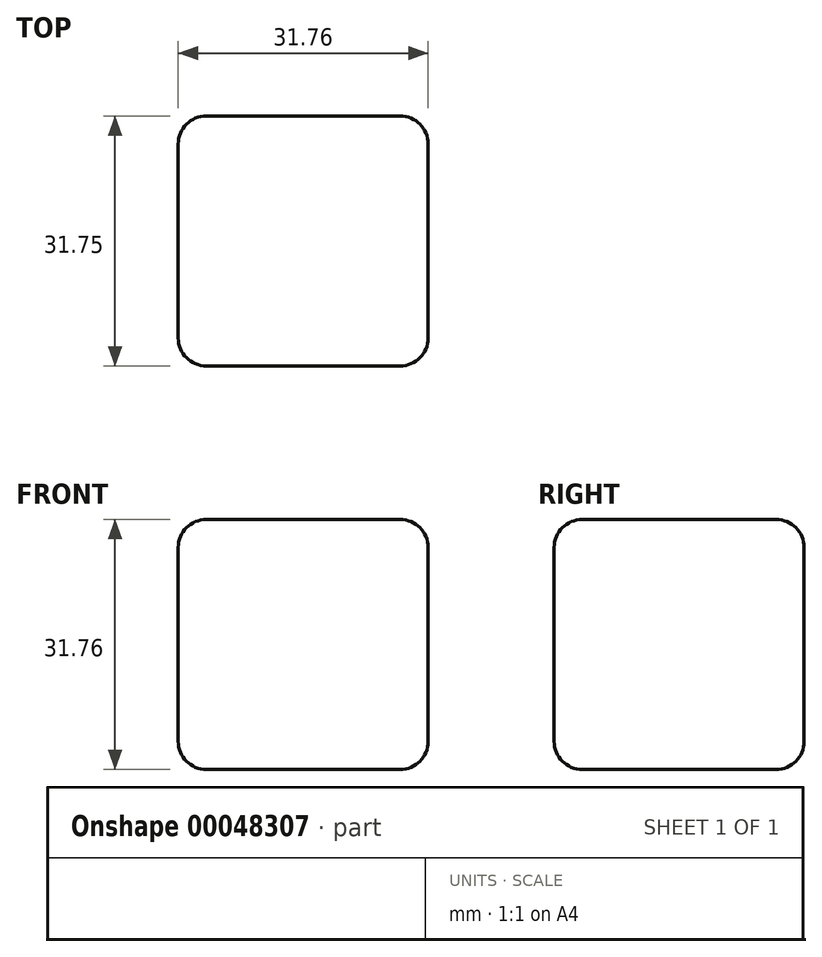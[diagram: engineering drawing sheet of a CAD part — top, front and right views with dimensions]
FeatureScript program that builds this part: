
annotation { "Feature Type Name" : "Feature", "Feature Type Description" : "" }
export const myFeature = defineFeature(function(context is Context, id is Id, definition is map)
    precondition{}
    {
        {
            var Q0;
            Q0=qCreatedBy(makeId("Front.planeOp"),FACE);
            var sketch = newSketch(context, id + "F0", { "sketchPlane" : qUnion([Q0])});
            skLineSegment(sketch, "E0.rect.bottom", {"start": v(15.88, -15.87) * mm, "end": v(-15.88, -15.88) * mm});
            skLineSegment(sketch, "E0.rect.top", {"start": v(15.88, 15.88) * mm, "end": v(-15.88, 15.87) * mm});
            skLineSegment(sketch, "E0.rect.left", {"start": v(15.88, -15.87) * mm, "end": v(15.88, 15.88) * mm});
            skLineSegment(sketch, "E0.rect.right", {"start": v(-15.88, -15.88) * mm, "end": v(-15.88, 15.87) * mm});
            skPoint(sketch, "E0.rect.middle", {"position": v(0, 0) * mm});
            skSolve(sketch);
        }
        {
            var Q0;
            Q0=makeQuery(id+"F0.imprint","IMPRINT",FACE,{"disambiguationData":[TD([[makeQuery(id+"F0.imprint","IMPRINT",EDGE,{"derivedFrom":sQuery(id+"F0.wireOp",EDGE,"E0.rect.bottom")}),-1.0]])]});
            extrude(context, id + "F1", {"entities" : qUnion([Q0]), "depth" : 31.75 * mm});
        }
        {
            var Q0;
            Q0=makeQuery(id+"F1.opExtrude","SWEPT_EDGE",EDGE,{"disambiguationData":[OSD([sQuery(id+"F0.wireOp",EDGE,"E0.rect.bottom"),sQuery(id+"F0.wireOp",EDGE,"E0.rect.left")])]});
            var Q1;
            Q1=makeQuery(id+"F1.opExtrude","CAP_FACE",FACE,{"disambiguationData":[OSD([sQuery(id+"F0.wireOp",EDGE,"E0.rect.bottom"),sQuery(id+"F0.wireOp",EDGE,"E0.rect.top"),sQuery(id+"F0.wireOp",EDGE,"E0.rect.left"),sQuery(id+"F0.wireOp",EDGE,"E0.rect.right")])],"isStart":true});
            var Q2;
            Q2=makeQuery(id+"F1.opExtrude","SWEPT_EDGE",EDGE,{"disambiguationData":[OSD([sQuery(id+"F0.wireOp",EDGE,"E0.rect.bottom"),sQuery(id+"F0.wireOp",EDGE,"E0.rect.right")])]});
            var Q3;
            Q3=makeQuery(id+"F1.opExtrude","CAP_FACE",FACE,{"disambiguationData":[OSD([sQuery(id+"F0.wireOp",EDGE,"E0.rect.bottom"),sQuery(id+"F0.wireOp",EDGE,"E0.rect.top"),sQuery(id+"F0.wireOp",EDGE,"E0.rect.left"),sQuery(id+"F0.wireOp",EDGE,"E0.rect.right")])],"isStart":false});
            var Q4;
            Q4=makeQuery(id+"F1.opExtrude","SWEPT_EDGE",EDGE,{"disambiguationData":[OSD([sQuery(id+"F0.wireOp",EDGE,"E0.rect.top"),sQuery(id+"F0.wireOp",EDGE,"E0.rect.left")])]});
            var Q5;
            Q5=makeQuery(id+"F1.opExtrude","SWEPT_FACE",FACE,{"disambiguationData":[OSD([sQuery(id+"F0.wireOp",EDGE,"E0.rect.top")])]});
            var Q6;
            Q6=makeQuery(id+"F1.opExtrude","SWEPT_EDGE",EDGE,{"disambiguationData":[OSD([sQuery(id+"F0.wireOp",EDGE,"E0.rect.top"),sQuery(id+"F0.wireOp",EDGE,"E0.rect.right")])]});
            var Q7;
            Q7=makeQuery(id+"F1.opExtrude","SWEPT_FACE",FACE,{"disambiguationData":[OSD([sQuery(id+"F0.wireOp",EDGE,"E0.rect.left")])]});
            var Q8;
            Q8=makeQuery(id+"F1.opExtrude","CAP_EDGE",EDGE,{"disambiguationData":[OSD([sQuery(id+"F0.wireOp",EDGE,"E0.rect.bottom")])],"isStart":false});
            var Q9;
            Q9=makeQuery(id+"F1.opExtrude","CAP_EDGE",EDGE,{"disambiguationData":[OSD([sQuery(id+"F0.wireOp",EDGE,"E0.rect.top")])],"isStart":true});
            var Q10;
            Q10=makeQuery(id+"F1.opExtrude","CAP_EDGE",EDGE,{"disambiguationData":[OSD([sQuery(id+"F0.wireOp",EDGE,"E0.rect.top")])],"isStart":false});
            var Q11;
            Q11=makeQuery(id+"F1.opExtrude","CAP_EDGE",EDGE,{"disambiguationData":[OSD([sQuery(id+"F0.wireOp",EDGE,"E0.rect.left")])],"isStart":false});
            var Q12;
            Q12=makeQuery(id+"F1.opExtrude","CAP_EDGE",EDGE,{"disambiguationData":[OSD([sQuery(id+"F0.wireOp",EDGE,"E0.rect.right")])],"isStart":false});
            var Q13;
            Q13=makeQuery(id+"F1.opExtrude","SWEPT_FACE",FACE,{"disambiguationData":[OSD([sQuery(id+"F0.wireOp",EDGE,"E0.rect.bottom")])]});
            var Q14;
            Q14=makeQuery(id+"F1.opExtrude","CAP_EDGE",EDGE,{"disambiguationData":[OSD([sQuery(id+"F0.wireOp",EDGE,"E0.rect.bottom")])],"isStart":true});
            var Q15;
            Q15=makeQuery(id+"F1.opExtrude","SWEPT_FACE",FACE,{"disambiguationData":[OSD([sQuery(id+"F0.wireOp",EDGE,"E0.rect.right")])]});
            var Q16;
            Q16=makeQuery(id+"F1.opExtrude","CAP_EDGE",EDGE,{"disambiguationData":[OSD([sQuery(id+"F0.wireOp",EDGE,"E0.rect.left")])],"isStart":true});
            var Q17;
            Q17=makeQuery(id+"F1.opExtrude","CAP_EDGE",EDGE,{"disambiguationData":[OSD([sQuery(id+"F0.wireOp",EDGE,"E0.rect.right")])],"isStart":true});
            fillet(context, id + "F2", {"entities" : qUnion([Q0, Q1, Q2, Q3, Q4, Q5, Q6, Q7, Q8, Q9, Q10, Q11, Q12, Q13, Q14, Q15, Q16, Q17]), "radius" : 3.56 * mm, "tangentPropagation" : true, "allowEdgeOverflow" : false});
        }
    });
